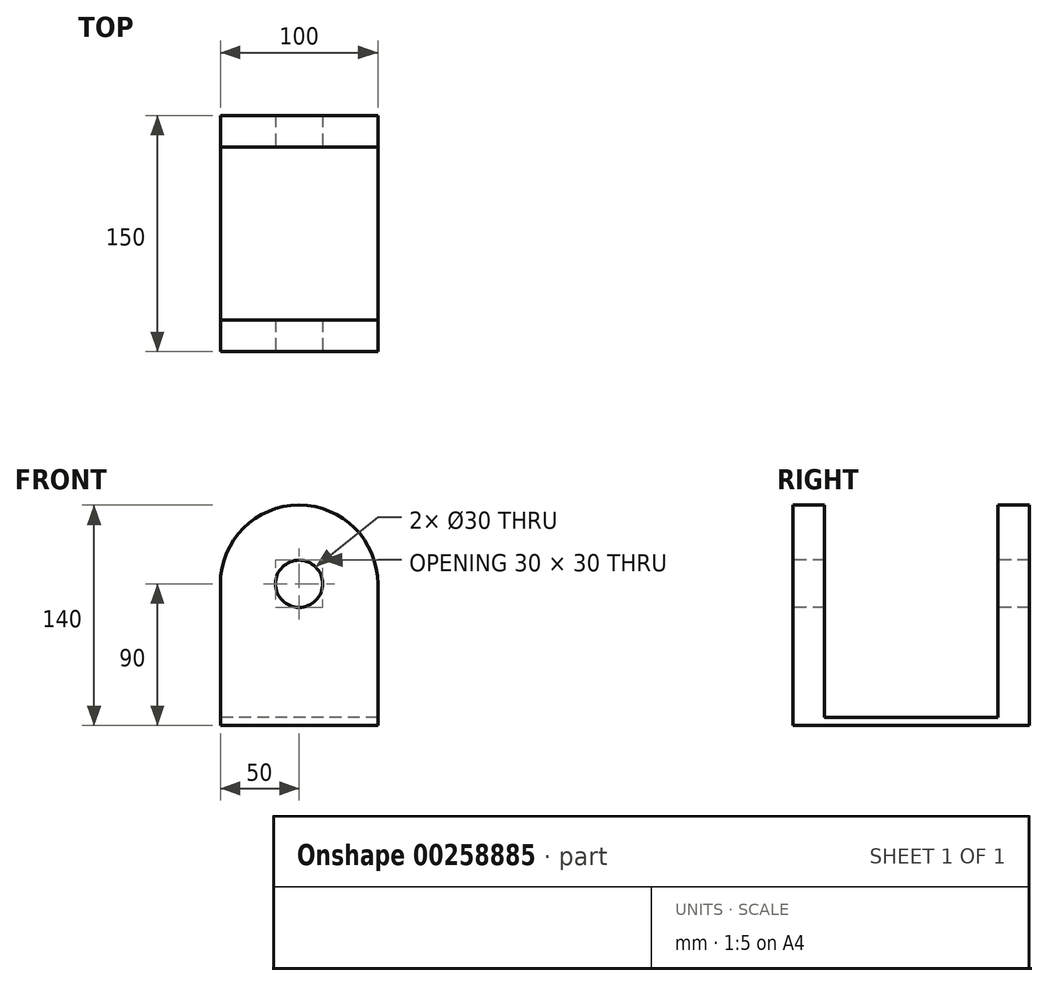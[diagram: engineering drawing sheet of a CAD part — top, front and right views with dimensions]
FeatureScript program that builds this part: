
annotation { "Feature Type Name" : "Feature", "Feature Type Description" : "" }
export const myFeature = defineFeature(function(context is Context, id is Id, definition is map)
    precondition{}
    {
        {
            var Q0;
            Q0=qCreatedBy(makeId("Front.planeOp"),FACE);
            var sketch = newSketch(context, id + "F0", { "sketchPlane" : qUnion([Q0])});
            skLineSegment(sketch, "E0", {"start": v(0, 0) * mm, "end": v(0, 5) * mm});
            skLineSegment(sketch, "E1", {"start": v(0, 5) * mm, "end": v(100, 5) * mm});
            skLineSegment(sketch, "E2", {"start": v(100, 5) * mm, "end": v(100, 0) * mm});
            skLineSegment(sketch, "E3", {"start": v(100, 0) * mm, "end": v(0, 0) * mm});
            skLineSegment(sketch, "E4", {"start": v(0, 5) * mm, "end": v(0, 90) * mm});
            skLineSegment(sketch, "E5", {"start": v(0, 90) * mm, "end": v(100, 90) * mm, "construction": true});
            skLineSegment(sketch, "E6", {"start": v(100, 90) * mm, "end": v(100, 5) * mm});
            skArc(sketch, "E7", {"start": v(100, 90) * mm, "mid": v(50, 140) * mm, "end": v(0, 90) * mm});
            skCircle(sketch, "E8", {"center": v(50, 90) * mm, "radius": 15 * mm});
            skSolve(sketch);
        }
        {
            var Q0;
            Q0=qCreatedBy(makeId("Right.planeOp"),FACE);
            var sketch = newSketch(context, id + "F1", { "sketchPlane" : qUnion([Q0])});
            skLineSegment(sketch, "E9", {"start": v(0, 0) * mm, "end": v(150, 0) * mm});
            skLineSegment(sketch, "E10", {"start": v(0, 0) * mm, "end": v(0, 5) * mm});
            skLineSegment(sketch, "E11", {"start": v(0, 5) * mm, "end": v(150, 5) * mm});
            skLineSegment(sketch, "E12", {"start": v(150, 5) * mm, "end": v(150, 0) * mm});
            skLineSegment(sketch, "E13", {"start": v(0, 5) * mm, "end": v(0, 205) * mm});
            skLineSegment(sketch, "E14", {"start": v(0, 205) * mm, "end": v(20, 205) * mm});
            skLineSegment(sketch, "E15", {"start": v(20, 205) * mm, "end": v(20, 5) * mm});
            skLineSegment(sketch, "E16", {"start": v(150, 5) * mm, "end": v(150, 205) * mm});
            skLineSegment(sketch, "E17", {"start": v(150, 205) * mm, "end": v(130, 205) * mm});
            skLineSegment(sketch, "E18", {"start": v(130, 205) * mm, "end": v(130, 5) * mm});
            skSolve(sketch);
        }
        {
            var Q0;
            Q0=makeQuery(id+"F0.imprint","IMPRINT",FACE,{"disambiguationData":[TD([[makeQuery(id+"F0.imprint","IMPRINT",EDGE,{"derivedFrom":sQuery(id+"F0.wireOp",EDGE,"E1")}),1.0]])]});
            var Q1;
            Q1=makeQuery(id+"F0.imprint","IMPRINT",FACE,{"disambiguationData":[TD([[makeQuery(id+"F0.imprint","IMPRINT",EDGE,{"derivedFrom":sQuery(id+"F0.wireOp",EDGE,"E0")}),-1.0]])]});
            extrude(context, id + "F2", {"entities" : qUnion([Q0, Q1]), "oppositeDirection" : true, "depth" : 150 * mm});
        }
        {
            var Q0;
            Q0 = qSketchRegion(id + "F1", true);
            extrude(context, id + "F3", {"entities" : qUnion([Q0]), "operationType" : NewBodyOperationType.INTERSECT, "depth" : 116.7 * mm});
        }
    });
